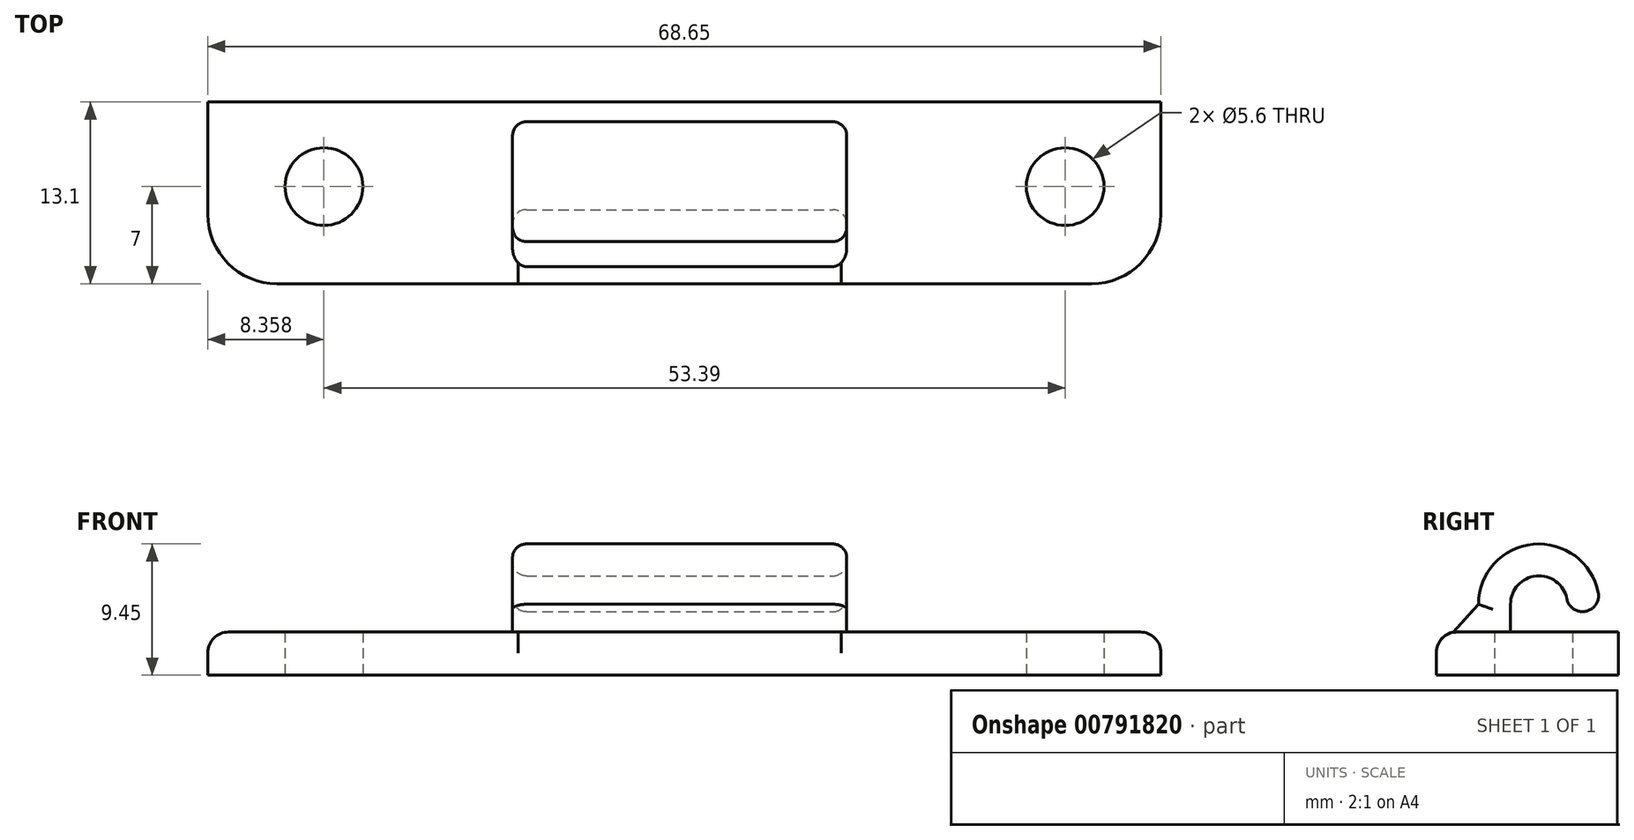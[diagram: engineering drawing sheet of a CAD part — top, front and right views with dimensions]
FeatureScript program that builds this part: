
annotation { "Feature Type Name" : "Feature", "Feature Type Description" : "" }
export const myFeature = defineFeature(function(context is Context, id is Id, definition is map)
    precondition{}
    {
        {
            var Q0;
            Q0=qCreatedBy(makeId("Top.planeOp"),FACE);
            var sketch = newSketch(context, id + "F0", { "sketchPlane" : qUnion([Q0])});
            skCircle(sketch, "E0", {"center": v(-17.35, 21.4) * mm, "radius": 2.8 * mm});
            skLineSegment(sketch, "E1", {"start": v(36.74, 27.5) * mm, "end": v(36.74, 21.3) * mm});
            skCircle(sketch, "E2", {"center": v(36.04, 21.4) * mm, "radius": 2.8 * mm});
            skPoint(sketch, "E3.visualSharp", {"position": v(-25.71, 27.5) * mm});
            skPoint(sketch, "E4.visualSharp", {"position": v(42.94, 27.5) * mm});
            skLineSegment(sketch, "E5", {"start": v(-25.71, 27.5) * mm, "end": v(-25.71, 22.5) * mm});
            skLineSegment(sketch, "E6", {"start": v(-20.71, 27.5) * mm, "end": v(-25.71, 27.5) * mm});
            skPoint(sketch, "E7.visualSharp", {"position": v(-25.71, 14.4) * mm});
            skArc(sketch, "E7.filletArc", {"start": v(-25.71, 19.4) * mm, "mid": v(-24.25, 15.86) * mm, "end": v(-20.71, 14.4) * mm});
            skLineSegment(sketch, "E8", {"start": v(38.29, 27.5) * mm, "end": v(42.94, 27.5) * mm});
            skLineSegment(sketch, "E9", {"start": v(42.94, 22.5) * mm, "end": v(42.94, 27.5) * mm});
            skPoint(sketch, "E10.visualSharp", {"position": v(42.94, 14.4) * mm});
            skArc(sketch, "E10.filletArc", {"start": v(37.94, 14.4) * mm, "mid": v(41.47, 15.86) * mm, "end": v(42.94, 19.4) * mm});
            skLineSegment(sketch, "E11", {"start": v(-25.71, 22.5) * mm, "end": v(-25.71, 19.4) * mm});
            skLineSegment(sketch, "E12", {"start": v(42.94, 22.5) * mm, "end": v(42.94, 19.4) * mm});
            skLineSegment(sketch, "E13", {"start": v(38.29, 27.5) * mm, "end": v(-20.71, 27.5) * mm});
            skLineSegment(sketch, "E14", {"start": v(-20.71, 14.4) * mm, "end": v(37.94, 14.4) * mm});
            skSolve(sketch);
        }
        {
            var Q0;
            Q0=qSketchRegion(id+"F0",true);
            extrude(context, id + "F1", {"entities" : qUnion([Q0]), "depth" : 3.1 * mm, "offsetDistance" : 25 * mm});
        }
        {
            var Q0;
            Q0=makeQuery(id+"F1.opExtrude","CAP_FACE",FACE,{"disambiguationData":[OSD([sQuery(id+"F0.wireOp",EDGE,"fae1df17-a2d7-4f6f-ac98-689a16ca2aa0.bottom"),sQuery(id+"F0.wireOp",EDGE,"E0"),sQuery(id+"F0.wireOp",EDGE,"E2"),sQuery(id+"F0.wireOp",EDGE,"F014CPc6-vz4U-GeCE-7854-YxV2qlxx2HBI"),sQuery(id+"F0.wireOp",EDGE,"oqsTX8BA-GUAt-ULMf-udCf-k8zS8YHXaQx7"),sQuery(id+"F0.wireOp",EDGE,"E5"),sQuery(id+"F0.wireOp",EDGE,"E6"),sQuery(id+"F0.wireOp",EDGE,"E7.filletArc"),sQuery(id+"F0.wireOp",EDGE,"E8"),sQuery(id+"F0.wireOp",EDGE,"E9"),sQuery(id+"F0.wireOp",EDGE,"boUDxhqq-Myw8-zXRC-cQ7O-OSDsYNN7bkR1"),sQuery(id+"F0.wireOp",EDGE,"Qmjh4y7b-Kf5U-xwWD-JW0z-h2leIeaRO661"),sQuery(id+"F0.wireOp",EDGE,"AKGd9Xzg-GUwK-bWbS-QEfH-SZGkE9dWEIcB"),sQuery(id+"F0.wireOp",EDGE,"A2VAHK38-QV2u-fNEz-uaTx-NxCy4vqKou6f"),sQuery(id+"F0.wireOp",EDGE,"0aa0c002-397a-412f-b6f0-cecf4b393b0d.filletArc"),sQuery(id+"F0.wireOp",EDGE,"e087cdcd-00e5-4b3d-8e79-89354ac833ec.filletArc"),sQuery(id+"F0.wireOp",EDGE,"1e3fda17-eca6-43e5-b7fb-2e88497f6e6a.filletArc")])],"isStart":false});
            var sketch = newSketch(context, id + "F2", { "sketchPlane" : qUnion([Q0])});
            skLineSegment(sketch, "E15.bottom", {"start": v(-3.76, 19.74) * mm, "end": v(20.3, 19.74) * mm});
            skLineSegment(sketch, "E15.top", {"start": v(-3.76, 17.44) * mm, "end": v(20.3, 17.44) * mm});
            skLineSegment(sketch, "E15.left", {"start": v(-3.76, 19.74) * mm, "end": v(-3.76, 17.44) * mm});
            skLineSegment(sketch, "E15.right", {"start": v(20.3, 19.74) * mm, "end": v(20.3, 17.44) * mm});
            skSolve(sketch);
        }
        {
            var Q0;
            Q0=qSketchRegion(id+"F2",true);
            extrude(context, id + "F3", {"entities" : qUnion([Q0]), "operationType" : NewBodyOperationType.ADD, "depth" : 2 * mm, "offsetDistance" : 25 * mm});
        }
        {
            var Q0;
            Q0=makeQuery(id+"F3.opExtrude","CAP_FACE",FACE,{"disambiguationData":[OSD([sQuery(id+"F2.wireOp",EDGE,"E15.bottom"),sQuery(id+"F2.wireOp",EDGE,"E15.top"),sQuery(id+"F2.wireOp",EDGE,"E15.left"),sQuery(id+"F2.wireOp",EDGE,"E15.right")])],"isStart":false});
            var sketch = newSketch(context, id + "F4", { "sketchPlane" : qUnion([Q0])});
            skLineSegment(sketch, "E16", {"start": v(-3.76, 21.79) * mm, "end": v(20.3, 21.79) * mm});
            skSolve(sketch);
        }
        {
            var Q0;
            Q0=makeQuery(id+"F3.opExtrude","CAP_FACE",FACE,{"disambiguationData":[OSD([sQuery(id+"F2.wireOp",EDGE,"E15.bottom"),sQuery(id+"F2.wireOp",EDGE,"E15.top"),sQuery(id+"F2.wireOp",EDGE,"E15.left"),sQuery(id+"F2.wireOp",EDGE,"E15.right")])],"isStart":false});
            var Q1;
            Q1=sQuery(id+"F4.wireOp",EDGE,"E16");
            revolve(context, id + "F5", {"operationType" : NewBodyOperationType.ADD, "surfaceOperationType" : NewSurfaceOperationType.NEW, "entities" : qUnion([Q0]), "axis" : qUnion([Q1]), "revolveType" : RevolveType.ONE_DIRECTION, "oppositeDirection" : true, "angle" : 190 * degree});
        }
        {
            var Q0;
            Q0=makeQuery(id+"F5.opRevolve","CAP_EDGE",EDGE,{"disambiguationData":[OSD([sQuery(id+"F2.wireOp",EDGE,"E15.bottom")])],"isStart":false});
            var Q1;
            Q1=makeQuery(id+"F5.opRevolve","CAP_EDGE",EDGE,{"disambiguationData":[OSD([sQuery(id+"F2.wireOp",EDGE,"E15.top")])],"isStart":false});
            fillet(context, id + "F6", {"entities" : qUnion([Q0, Q1]), "radius" : 1.15 * mm, "tangentPropagation" : true, "allowEdgeOverflow" : false});
        }
        {
            var Q0;
            {var subQ0=sQuery(id+"F2.wireOp",EDGE,"E15.left");Q0=makeQuery(id+"F5.boolean.opBoolean","MERGE",FACE,{"derivedFrom":[makeQuery(id+"F3.opExtrude","SWEPT_FACE",FACE,{"disambiguationData":[OSD([subQ0])]}),makeQuery(id+"F5.opRevolve","SWEPT_FACE",FACE,{"disambiguationData":[OSD([subQ0])]})]});}
            var sketch = newSketch(context, id + "F7", { "sketchPlane" : qUnion([Q0])});
            skLineSegment(sketch, "E17", {"start": v(-17.44, 5.1) * mm, "end": v(-15.64, 3.1) * mm});
            skLineSegment(sketch, "E18", {"start": v(-15.64, 3.1) * mm, "end": v(-17.44, 3.1) * mm});
            skLineSegment(sketch, "E19", {"start": v(-17.44, 5.1) * mm, "end": v(-17.44, 3.1) * mm});
            skSolve(sketch);
        }
        {
            var Q0;
            Q0=qSketchRegion(id+"F7",true);
            extrude(context, id + "F8", {"entities" : qUnion([Q0]), "operationType" : NewBodyOperationType.ADD, "oppositeDirection" : true, "depth" : 24.07 * mm, "offsetDistance" : 25 * mm});
        }
        {
            var Q0;
            Q0=makeQuery(id+"F8.opExtrude","CAP_EDGE",EDGE,{"disambiguationData":[OSD([sQuery(id+"F7.wireOp",EDGE,"E17")])],"isStart":true});
            var Q1;
            Q1=makeQuery(id+"F5.opRevolve","SWEPT_EDGE",EDGE,{"disambiguationData":[OSD([sQuery(id+"F2.wireOp",EDGE,"E15.top"),sQuery(id+"F2.wireOp",EDGE,"E15.left")])]});
            var Q2;
            Q2=makeQuery(id+"F8.opExtrude","CAP_EDGE",EDGE,{"disambiguationData":[OSD([sQuery(id+"F7.wireOp",EDGE,"E17")])],"isStart":false});
            var Q3;
            Q3=makeQuery(id+"F5.opRevolve","SWEPT_EDGE",EDGE,{"disambiguationData":[OSD([sQuery(id+"F2.wireOp",EDGE,"E15.top"),sQuery(id+"F2.wireOp",EDGE,"E15.right")])]});
            fillet(context, id + "F9", {"entities" : qUnion([Q0, Q1, Q2, Q3]), "radius" : 1 * mm, "tangentPropagation" : true, "defaultsChanged" : true, "vertexSettings" : [], "allowEdgeOverflow" : false});
        }
        {
            var Q0;
            Q0=makeQuery(id+"F1.opExtrude","CAP_EDGE",EDGE,{"disambiguationData":[OSD([sQuery(id+"F0.wireOp",EDGE,"CgDLwSNg-zf42-mTSh-7aab-tOykAud3vaq0")])],"isStart":false});
            var Q1;
            Q1=makeQuery(id+"F1.opExtrude","CAP_EDGE",EDGE,{"disambiguationData":[OSD([sQuery(id+"F0.wireOp",EDGE,"E14")])],"isStart":false});
            fillet(context, id + "F10", {"entities" : qUnion([Q0, Q1]), "radius" : 1.5 * mm, "tangentPropagation" : true, "defaultsChanged" : false, "vertexSettings" : [], "allowEdgeOverflow" : false});
        }
    });
